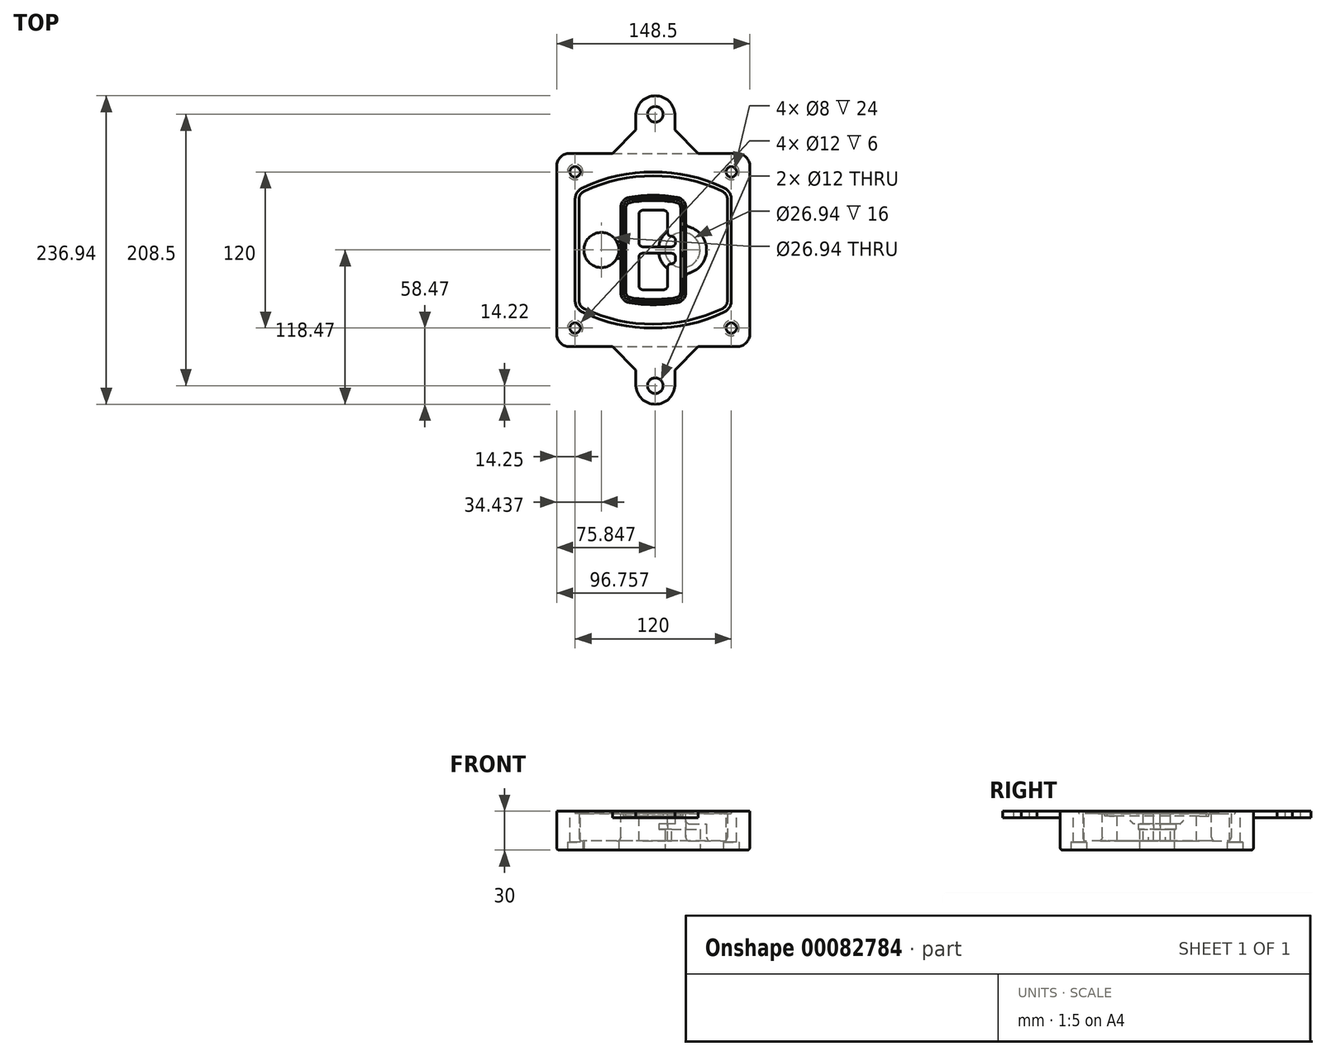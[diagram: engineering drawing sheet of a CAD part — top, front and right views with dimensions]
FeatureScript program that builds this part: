
annotation { "Feature Type Name" : "Feature", "Feature Type Description" : "" }
export const myFeature = defineFeature(function(context is Context, id is Id, definition is map)
    precondition{}
    {
        {
            var Q0;
            Q0=qCreatedBy(makeId("Top.planeOp"),FACE);
            var sketch = newSketch(context, id + "F0", { "sketchPlane" : qUnion([Q0])});
            skPoint(sketch, "E0.rect.middle", {"position": v(0, 0) * mm});
            skLineSegment(sketch, "E1.bottom", {"start": v(-64.25, -74.25) * mm, "end": v(64.25, -74.25) * mm});
            skLineSegment(sketch, "E1.top", {"start": v(-64.25, 74.25) * mm, "end": v(64.25, 74.25) * mm});
            skLineSegment(sketch, "E1.left", {"start": v(-74.25, -64.25) * mm, "end": v(-74.25, 64.25) * mm});
            skLineSegment(sketch, "E1.right", {"start": v(74.25, -64.25) * mm, "end": v(74.25, 64.25) * mm});
            skLineSegment(sketch, "E2", {"start": v(-74.25, 74.25) * mm, "end": v(74.25, -74.25) * mm, "construction": true});
            skLineSegment(sketch, "E3", {"start": v(74.25, 74.25) * mm, "end": v(-74.25, -74.25) * mm, "construction": true});
            skCircle(sketch, "E4", {"center": v(-60, 60) * mm, "radius": 4 * mm});
            skCircle(sketch, "E5", {"center": v(60, 60) * mm, "radius": 4 * mm});
            skCircle(sketch, "E6", {"center": v(60, -60) * mm, "radius": 4 * mm});
            skCircle(sketch, "E7", {"center": v(-60, -60) * mm, "radius": 4 * mm});
            skLineSegment(sketch, "E8", {"start": v(-60, 60) * mm, "end": v(60, 60) * mm, "construction": true});
            skLineSegment(sketch, "E9", {"start": v(60, 60) * mm, "end": v(60, -60) * mm, "construction": true});
            skLineSegment(sketch, "E10", {"start": v(60, -60) * mm, "end": v(-60, -60) * mm, "construction": true});
            skLineSegment(sketch, "E11", {"start": v(-60, -60) * mm, "end": v(-60, 60) * mm, "construction": true});
            skLineSegment(sketch, "E12", {"start": v(-60, 38.83) * mm, "end": v(-60, -38.83) * mm});
            skLineSegment(sketch, "E13", {"start": v(60, 38.83) * mm, "end": v(60, -38.83) * mm});
            skArc(sketch, "E14", {"start": v(54.26, 47.88) * mm, "mid": v(0, 60) * mm, "end": v(-54.26, 47.88) * mm});
            skArc(sketch, "E15", {"start": v(-54.26, -47.88) * mm, "mid": v(0, -60) * mm, "end": v(54.26, -47.88) * mm});
            skLineSegment(sketch, "E16", {"start": v(-60, 0) * mm, "end": v(60, 0) * mm, "construction": true});
            skPoint(sketch, "E17.visualSharp", {"position": v(-60, -45) * mm});
            skArc(sketch, "E17.filletArc", {"start": v(-60, -38.83) * mm, "mid": v(-58.44, -44.2) * mm, "end": v(-54.26, -47.88) * mm});
            skPoint(sketch, "E18.visualSharp", {"position": v(-60, 45) * mm});
            skArc(sketch, "E18.filletArc", {"start": v(-54.26, 47.88) * mm, "mid": v(-58.44, 44.2) * mm, "end": v(-60, 38.83) * mm});
            skPoint(sketch, "E19.visualSharp", {"position": v(60, 45) * mm});
            skArc(sketch, "E19.filletArc", {"start": v(60, 38.83) * mm, "mid": v(58.44, 44.2) * mm, "end": v(54.26, 47.88) * mm});
            skPoint(sketch, "E20.visualSharp", {"position": v(60, -45) * mm});
            skArc(sketch, "E20.filletArc", {"start": v(54.26, -47.88) * mm, "mid": v(58.44, -44.2) * mm, "end": v(60, -38.83) * mm});
            skPoint(sketch, "E21.visualSharp", {"position": v(-74.25, 74.25) * mm});
            skArc(sketch, "E21.filletArc", {"start": v(-64.25, 74.25) * mm, "mid": v(-71.32, 71.32) * mm, "end": v(-74.25, 64.25) * mm});
            skPoint(sketch, "E22.visualSharp", {"position": v(74.25, 74.25) * mm});
            skArc(sketch, "E22.filletArc", {"start": v(74.25, 64.25) * mm, "mid": v(71.32, 71.32) * mm, "end": v(64.25, 74.25) * mm});
            skPoint(sketch, "E23.visualSharp", {"position": v(74.25, -74.25) * mm});
            skArc(sketch, "E23.filletArc", {"start": v(64.25, -74.25) * mm, "mid": v(71.32, -71.32) * mm, "end": v(74.25, -64.25) * mm});
            skPoint(sketch, "E24.visualSharp", {"position": v(-74.25, -74.25) * mm});
            skArc(sketch, "E24.filletArc", {"start": v(-74.25, -64.25) * mm, "mid": v(-71.32, -71.32) * mm, "end": v(-64.25, -74.25) * mm});
            skArc(sketch, "E25.0", {"start": v(57, 38.83) * mm, "mid": v(55.9, 42.58) * mm, "end": v(52.98, 45.17) * mm});
            skLineSegment(sketch, "E25.1", {"start": v(57, 38.83) * mm, "end": v(57, -38.83) * mm});
            skArc(sketch, "E25.2", {"start": v(52.98, -45.17) * mm, "mid": v(55.9, -42.58) * mm, "end": v(57, -38.83) * mm});
            skArc(sketch, "E25.3", {"start": v(-52.98, -45.17) * mm, "mid": v(0, -57) * mm, "end": v(52.98, -45.17) * mm});
            skArc(sketch, "E25.4", {"start": v(-57, -38.83) * mm, "mid": v(-55.9, -42.58) * mm, "end": v(-52.98, -45.17) * mm});
            skArc(sketch, "E25.5", {"start": v(52.98, 45.17) * mm, "mid": v(0, 57) * mm, "end": v(-52.98, 45.17) * mm});
            skLineSegment(sketch, "E25.6", {"start": v(-57, 38.83) * mm, "end": v(-57, -38.83) * mm});
            skArc(sketch, "E25.7", {"start": v(-52.98, 45.17) * mm, "mid": v(-55.9, 42.58) * mm, "end": v(-57, 38.83) * mm});
            skArc(sketch, "E26.0", {"start": v(-55.96, 51.5) * mm, "mid": v(-61.82, 46.33) * mm, "end": v(-64, 38.83) * mm});
            skArc(sketch, "E26.1", {"start": v(55.96, 51.5) * mm, "mid": v(0, 64) * mm, "end": v(-55.96, 51.5) * mm});
            skArc(sketch, "E26.2", {"start": v(64, 38.83) * mm, "mid": v(61.82, 46.33) * mm, "end": v(55.96, 51.5) * mm});
            skLineSegment(sketch, "E26.3", {"start": v(64, 38.83) * mm, "end": v(64, -38.83) * mm});
            skArc(sketch, "E26.4", {"start": v(55.96, -51.5) * mm, "mid": v(61.82, -46.33) * mm, "end": v(64, -38.83) * mm});
            skLineSegment(sketch, "E26.5", {"start": v(-64, 38.83) * mm, "end": v(-64, -38.83) * mm});
            skArc(sketch, "E26.6", {"start": v(-55.96, -51.5) * mm, "mid": v(0, -64) * mm, "end": v(55.96, -51.5) * mm});
            skArc(sketch, "E26.7", {"start": v(-64, -38.83) * mm, "mid": v(-61.82, -46.33) * mm, "end": v(-55.96, -51.5) * mm});
            skSolve(sketch);
        }
        {
            var Q0;
            Q0=makeQuery(id+"F0.imprint","IMPRINT",FACE,{"disambiguationData":[TD([[makeQuery(id+"F0.imprint","IMPRINT",EDGE,{"derivedFrom":sQuery(id+"F0.wireOp",EDGE,"E1.bottom")}),1.0]])]});
            var Q1;
            Q1=makeQuery(id+"F0.imprint","IMPRINT",FACE,{"disambiguationData":[TD([[makeQuery(id+"F0.imprint","IMPRINT",EDGE,{"derivedFrom":sQuery(id+"F0.wireOp",EDGE,"E12")}),1.0]])]});
            var Q2;
            Q2=makeQuery(id+"F0.imprint","IMPRINT",FACE,{"disambiguationData":[TD([[makeQuery(id+"F0.imprint","IMPRINT",EDGE,{"derivedFrom":sQuery(id+"F0.wireOp",EDGE,"E25.0")}),1.0]])]});
            var Q3;
            Q3=makeQuery(id+"F0.imprint","IMPRINT",FACE,{"disambiguationData":[TD([[makeQuery(id+"F0.imprint","IMPRINT",EDGE,{"derivedFrom":sQuery(id+"F0.wireOp",EDGE,"E12")}),-1.0]])]});
            extrude(context, id + "F1", {"entities" : qUnion([Q0, Q1, Q2, Q3]), "oppositeDirection" : true, "depth" : 25 * mm});
        }
        {
            var Q0;
            Q0=makeQuery(id+"F0.imprint","IMPRINT",FACE,{"disambiguationData":[TD([[makeQuery(id+"F0.imprint","IMPRINT",EDGE,{"derivedFrom":sQuery(id+"F0.wireOp",EDGE,"E12")}),1.0]])]});
            extrude(context, id + "F2", {"entities" : qUnion([Q0]), "operationType" : NewBodyOperationType.ADD, "depth" : 3 * mm});
        }
        {
            var Q0;
            Q0=makeQuery(id+"F0.imprint","IMPRINT",FACE,{"disambiguationData":[TD([[makeQuery(id+"F0.imprint","IMPRINT",EDGE,{"derivedFrom":sQuery(id+"F0.wireOp",EDGE,"E25.0")}),1.0]])]});
            extrude(context, id + "F3", {"entities" : qUnion([Q0]), "operationType" : NewBodyOperationType.REMOVE, "oppositeDirection" : true, "depth" : 18 * mm});
        }
        {
            var Q0;
            Q0=makeQuery(id+"F2.opExtrude","CAP_FACE",FACE,{"disambiguationData":[OSD([sQuery(id+"F0.wireOp",EDGE,"E12"),sQuery(id+"F0.wireOp",EDGE,"E13"),sQuery(id+"F0.wireOp",EDGE,"E14"),sQuery(id+"F0.wireOp",EDGE,"E15"),sQuery(id+"F0.wireOp",EDGE,"E17.filletArc"),sQuery(id+"F0.wireOp",EDGE,"E18.filletArc"),sQuery(id+"F0.wireOp",EDGE,"E19.filletArc"),sQuery(id+"F0.wireOp",EDGE,"E20.filletArc"),sQuery(id+"F0.wireOp",EDGE,"E25.0"),sQuery(id+"F0.wireOp",EDGE,"E25.1"),sQuery(id+"F0.wireOp",EDGE,"E25.2"),sQuery(id+"F0.wireOp",EDGE,"E25.3"),sQuery(id+"F0.wireOp",EDGE,"E25.4"),sQuery(id+"F0.wireOp",EDGE,"E25.5"),sQuery(id+"F0.wireOp",EDGE,"E25.6"),sQuery(id+"F0.wireOp",EDGE,"E25.7")])],"isStart":false});
            var sketch = newSketch(context, id + "F4", { "sketchPlane" : qUnion([Q0])});
            skArc(sketch, "E27.0", {"start": v(-18.34, -40.45) * mm, "mid": v(0, -42) * mm, "end": v(18.34, -40.45) * mm});
            skArc(sketch, "E28.0", {"start": v(18.34, 40.45) * mm, "mid": v(0, 42) * mm, "end": v(-18.34, 40.45) * mm});
            skLineSegment(sketch, "E29", {"start": v(-25, 32.57) * mm, "end": v(-25, -32.57) * mm});
            skLineSegment(sketch, "E30", {"start": v(25, 32.57) * mm, "end": v(25, -32.57) * mm});
            skLineSegment(sketch, "E31", {"start": v(-25, 39.1) * mm, "end": v(25, 39.1) * mm, "construction": true});
            skLineSegment(sketch, "E32", {"start": v(-25, -39.1) * mm, "end": v(25, -39.1) * mm, "construction": true});
            skPoint(sketch, "E33.visualSharp", {"position": v(-25, 39.1) * mm});
            skArc(sketch, "E33.filletArc", {"start": v(-18.34, 40.45) * mm, "mid": v(-23.11, 37.73) * mm, "end": v(-25, 32.57) * mm});
            skPoint(sketch, "E34.visualSharp", {"position": v(25, 39.1) * mm});
            skArc(sketch, "E34.filletArc", {"start": v(25, 32.57) * mm, "mid": v(23.11, 37.73) * mm, "end": v(18.34, 40.45) * mm});
            skPoint(sketch, "E35.visualSharp", {"position": v(25, -39.1) * mm});
            skArc(sketch, "E35.filletArc", {"start": v(18.34, -40.45) * mm, "mid": v(23.11, -37.73) * mm, "end": v(25, -32.57) * mm});
            skPoint(sketch, "E36.visualSharp", {"position": v(-25, -39.1) * mm});
            skArc(sketch, "E36.filletArc", {"start": v(-25, -32.57) * mm, "mid": v(-23.11, -37.73) * mm, "end": v(-18.34, -40.45) * mm});
            skArc(sketch, "E37.0", {"start": v(52.98, 45.17) * mm, "mid": v(0, 57) * mm, "end": v(-52.98, 45.17) * mm});
            skArc(sketch, "E37.1", {"start": v(-52.98, 45.17) * mm, "mid": v(-55.9, 42.58) * mm, "end": v(-57, 38.83) * mm});
            skLineSegment(sketch, "E37.2", {"start": v(-57, 38.83) * mm, "end": v(-57, -38.83) * mm});
            skArc(sketch, "E37.3", {"start": v(-57, -38.83) * mm, "mid": v(-55.9, -42.58) * mm, "end": v(-52.98, -45.17) * mm});
            skArc(sketch, "E37.4", {"start": v(-52.98, -45.17) * mm, "mid": v(0, -57) * mm, "end": v(52.98, -45.17) * mm});
            skArc(sketch, "E37.5", {"start": v(52.98, -45.17) * mm, "mid": v(55.9, -42.58) * mm, "end": v(57, -38.83) * mm});
            skLineSegment(sketch, "E37.6", {"start": v(57, 38.83) * mm, "end": v(57, -38.83) * mm});
            skArc(sketch, "E37.7", {"start": v(57, 38.83) * mm, "mid": v(55.9, 42.58) * mm, "end": v(52.98, 45.17) * mm});
            skLineSegment(sketch, "E38.0", {"start": v(23, 32.57) * mm, "end": v(23, -32.57) * mm});
            skArc(sketch, "E38.1", {"start": v(18, -38.48) * mm, "mid": v(21.58, -36.44) * mm, "end": v(23, -32.57) * mm});
            skArc(sketch, "E38.2", {"start": v(-18, -38.48) * mm, "mid": v(0, -40) * mm, "end": v(18, -38.48) * mm});
            skArc(sketch, "E38.3", {"start": v(-23, -32.57) * mm, "mid": v(-21.58, -36.44) * mm, "end": v(-18, -38.48) * mm});
            skLineSegment(sketch, "E38.4", {"start": v(-23, 32.57) * mm, "end": v(-23, -32.57) * mm});
            skArc(sketch, "E38.5", {"start": v(23, 32.57) * mm, "mid": v(21.58, 36.44) * mm, "end": v(18, 38.48) * mm});
            skArc(sketch, "E38.6", {"start": v(-18, 38.48) * mm, "mid": v(-21.58, 36.44) * mm, "end": v(-23, 32.57) * mm});
            skArc(sketch, "E38.7", {"start": v(18, 38.48) * mm, "mid": v(0, 40) * mm, "end": v(-18, 38.48) * mm});
            skArc(sketch, "E39.0", {"start": v(21, 32.57) * mm, "mid": v(20.06, 35.15) * mm, "end": v(17.67, 36.5) * mm});
            skLineSegment(sketch, "E39.1", {"start": v(21, 32.57) * mm, "end": v(21, -32.57) * mm});
            skArc(sketch, "E39.2", {"start": v(17.67, -36.5) * mm, "mid": v(20.06, -35.15) * mm, "end": v(21, -32.57) * mm});
            skArc(sketch, "E39.3", {"start": v(-17.67, -36.5) * mm, "mid": v(0, -38) * mm, "end": v(17.67, -36.5) * mm});
            skArc(sketch, "E39.4", {"start": v(-21, -32.57) * mm, "mid": v(-20.06, -35.15) * mm, "end": v(-17.67, -36.5) * mm});
            skArc(sketch, "E39.5", {"start": v(17.67, 36.5) * mm, "mid": v(0, 38) * mm, "end": v(-17.67, 36.5) * mm});
            skLineSegment(sketch, "E39.6", {"start": v(-21, 32.57) * mm, "end": v(-21, -32.57) * mm});
            skArc(sketch, "E39.7", {"start": v(-17.67, 36.5) * mm, "mid": v(-20.06, 35.15) * mm, "end": v(-21, 32.57) * mm});
            skLineSegment(sketch, "E40", {"start": v(-25, 0) * mm, "end": v(25, 0) * mm, "construction": true});
            skLineSegment(sketch, "E41", {"start": v(-11, 5.5) * mm, "end": v(-11, 27.5) * mm});
            skLineSegment(sketch, "E42", {"start": v(-8, 30.5) * mm, "end": v(8, 30.5) * mm});
            skLineSegment(sketch, "E43", {"start": v(11, 27.5) * mm, "end": v(11, 13.5) * mm});
            skLineSegment(sketch, "E44", {"start": v(14, 10.5) * mm, "end": v(14, 10.5) * mm});
            skLineSegment(sketch, "E45", {"start": v(17, 7.5) * mm, "end": v(17, 5.5) * mm});
            skLineSegment(sketch, "E46", {"start": v(14, 2.5) * mm, "end": v(-8, 2.5) * mm});
            skPoint(sketch, "E47.visualSharp", {"position": v(-11, 30.5) * mm});
            skArc(sketch, "E47.filletArc", {"start": v(-8, 30.5) * mm, "mid": v(-10.12, 29.62) * mm, "end": v(-11, 27.5) * mm});
            skPoint(sketch, "E48.visualSharp", {"position": v(11, 30.5) * mm});
            skArc(sketch, "E48.filletArc", {"start": v(11, 27.5) * mm, "mid": v(10.12, 29.62) * mm, "end": v(8, 30.5) * mm});
            skPoint(sketch, "E49.visualSharp", {"position": v(11, 10.5) * mm});
            skArc(sketch, "E49.filletArc", {"start": v(11, 13.5) * mm, "mid": v(11.88, 11.38) * mm, "end": v(14, 10.5) * mm});
            skPoint(sketch, "E50.visualSharp", {"position": v(17, 10.5) * mm});
            skArc(sketch, "E50.filletArc", {"start": v(17, 7.5) * mm, "mid": v(16.12, 9.62) * mm, "end": v(14, 10.5) * mm});
            skPoint(sketch, "E51.visualSharp", {"position": v(17, 2.5) * mm});
            skArc(sketch, "E51.filletArc", {"start": v(14, 2.5) * mm, "mid": v(16.12, 3.38) * mm, "end": v(17, 5.5) * mm});
            skPoint(sketch, "E52.visualSharp", {"position": v(-11, 2.5) * mm});
            skArc(sketch, "E52.filletArc", {"start": v(-11, 5.5) * mm, "mid": v(-10.12, 3.38) * mm, "end": v(-8, 2.5) * mm});
            skLineSegment(sketch, "E53.0.MirrorCS", {"start": v(14, -2.5) * mm, "end": v(-8, -2.5) * mm});
            skArc(sketch, "E54.0.MirrorCS", {"start": v(-11, -5.5) * mm, "mid": v(-10.12, -3.38) * mm, "end": v(-8, -2.5) * mm});
            skLineSegment(sketch, "E55.0.MirrorCS", {"start": v(-11, -5.5) * mm, "end": v(-11, -27.5) * mm});
            skArc(sketch, "E56.0.MirrorCS", {"start": v(-8, -30.5) * mm, "mid": v(-10.12, -29.62) * mm, "end": v(-11, -27.5) * mm});
            skLineSegment(sketch, "E57.0.MirrorCS", {"start": v(-8, -30.5) * mm, "end": v(8, -30.5) * mm});
            skArc(sketch, "E58.0.MirrorCS", {"start": v(11, -27.5) * mm, "mid": v(10.12, -29.62) * mm, "end": v(8, -30.5) * mm});
            skLineSegment(sketch, "E59.0.MirrorCS", {"start": v(11, -27.5) * mm, "end": v(11, -13.5) * mm});
            skArc(sketch, "E60.0.MirrorCS", {"start": v(11, -13.5) * mm, "mid": v(11.88, -11.38) * mm, "end": v(14, -10.5) * mm});
            skArc(sketch, "E61.0.MirrorCS", {"start": v(17, -7.5) * mm, "mid": v(16.12, -9.62) * mm, "end": v(14, -10.5) * mm});
            skLineSegment(sketch, "E62.0.MirrorCS", {"start": v(17, -7.5) * mm, "end": v(17, -5.5) * mm});
            skArc(sketch, "E63.0.MirrorCS", {"start": v(14, -2.5) * mm, "mid": v(16.12, -3.38) * mm, "end": v(17, -5.5) * mm});
            skSolve(sketch);
        }
        {
            var Q0;
            Q0=makeQuery(id+"F4.imprint","IMPRINT",FACE,{"disambiguationData":[TD([[makeQuery(id+"F4.imprint","IMPRINT",EDGE,{"derivedFrom":sQuery(id+"F4.wireOp",EDGE,"E27.0")}),1.0]])]});
            var Q1;
            Q1=makeQuery(id+"F4.imprint","IMPRINT",FACE,{"disambiguationData":[TD([[makeQuery(id+"F4.imprint","IMPRINT",EDGE,{"derivedFrom":sQuery(id+"F4.wireOp",EDGE,"E38.0")}),-1.0]])]});
            var Q2;
            Q2=makeQuery(id+"F4.imprint","IMPRINT",FACE,{"disambiguationData":[TD([[makeQuery(id+"F4.imprint","IMPRINT",EDGE,{"derivedFrom":sQuery(id+"F4.wireOp",EDGE,"E39.0")}),1.0]])]});
            extrude(context, id + "F5", {"entities" : qUnion([Q0, Q1, Q2]), "operationType" : NewBodyOperationType.ADD, "endBound" : BoundingType.UP_TO_NEXT, "oppositeDirection" : true, "depth" : 25 * mm});
        }
        {
            var Q0;
            Q0=makeQuery(id+"F4.imprint","IMPRINT",FACE,{"disambiguationData":[TD([[makeQuery(id+"F4.imprint","IMPRINT",EDGE,{"derivedFrom":sQuery(id+"F4.wireOp",EDGE,"E38.0")}),-1.0]])]});
            extrude(context, id + "F6", {"entities" : qUnion([Q0]), "operationType" : NewBodyOperationType.REMOVE, "oppositeDirection" : true, "depth" : 2 * mm});
        }
        {
            var Q0;
            Q0=makeQuery(id+"F1.opExtrude","CAP_FACE",FACE,{"disambiguationData":[OSD([sQuery(id+"F0.wireOp",EDGE,"E1.bottom"),sQuery(id+"F0.wireOp",EDGE,"E1.top"),sQuery(id+"F0.wireOp",EDGE,"E1.left"),sQuery(id+"F0.wireOp",EDGE,"E1.right"),sQuery(id+"F0.wireOp",EDGE,"E4"),sQuery(id+"F0.wireOp",EDGE,"E5"),sQuery(id+"F0.wireOp",EDGE,"E6"),sQuery(id+"F0.wireOp",EDGE,"E7"),sQuery(id+"F0.wireOp",EDGE,"E21.filletArc"),sQuery(id+"F0.wireOp",EDGE,"E22.filletArc"),sQuery(id+"F0.wireOp",EDGE,"E23.filletArc"),sQuery(id+"F0.wireOp",EDGE,"E24.filletArc")])],"isStart":false});
            var sketch = newSketch(context, id + "F7", { "sketchPlane" : qUnion([Q0])});
            skCircle(sketch, "E64", {"center": v(22.5, 0) * mm, "radius": 13.47 * mm});
            skCircle(sketch, "E65", {"center": v(-39.81, 0) * mm, "radius": 13.47 * mm});
            skLineSegment(sketch, "E66", {"start": v(74.25, 0) * mm, "end": v(-74.25, 0) * mm});
            skCircle(sketch, "E67", {"center": v(22.5, 0) * mm, "radius": 18.47 * mm});
            skCircle(sketch, "E68", {"center": v(60, -60) * mm, "radius": 6 * mm});
            skCircle(sketch, "E69", {"center": v(-60, -60) * mm, "radius": 6 * mm});
            skCircle(sketch, "E70", {"center": v(-60, 60) * mm, "radius": 6 * mm});
            skCircle(sketch, "E71", {"center": v(60, 60) * mm, "radius": 6 * mm});
            skSolve(sketch);
        }
        {
            var Q0;
            {var subQ1=sQuery(id+"F7.wireOp",EDGE,"E66");var subQ4=sQuery(id+"F7.wireOp",EDGE,"E64");var subQ6=makeQuery(id+"F7.imprint","INTERSECT",VERTEX,{"disambiguationData":[OD(0.0)],"derivedFrom":[subQ4,subQ1]});Q0=makeQuery(id+"F7.imprint","IMPRINT",FACE,{"disambiguationData":[TD([[makeQuery(id+"F7.imprint","IMPRINT",EDGE,{"disambiguationData":[TD([[subQ6,-1.0]])],"derivedFrom":subQ4}),-1.0]])]});}
            var Q1;
            {var subQ0=sQuery(id+"F7.wireOp",EDGE,"E66");var subQ1=sQuery(id+"F7.wireOp",EDGE,"E64");var subQ3=makeQuery(id+"F7.imprint","INTERSECT",VERTEX,{"disambiguationData":[OD(0.0)],"derivedFrom":[subQ1,subQ0]});Q1=makeQuery(id+"F7.imprint","IMPRINT",FACE,{"disambiguationData":[TD([[makeQuery(id+"F7.imprint","IMPRINT",EDGE,{"disambiguationData":[TD([[subQ3,-1.0]])],"derivedFrom":subQ1}),1.0]])]});}
            var Q2;
            {var subQ0=sQuery(id+"F7.wireOp",EDGE,"E66");var subQ1=sQuery(id+"F7.wireOp",EDGE,"E64");var subQ3=makeQuery(id+"F7.imprint","INTERSECT",VERTEX,{"disambiguationData":[OD(0.0)],"derivedFrom":[subQ1,subQ0]});Q2=makeQuery(id+"F7.imprint","IMPRINT",FACE,{"disambiguationData":[TD([[makeQuery(id+"F7.imprint","IMPRINT",EDGE,{"disambiguationData":[TD([[subQ3,1.0]])],"derivedFrom":subQ1}),1.0]])]});}
            var Q3;
            {var subQ1=sQuery(id+"F7.wireOp",EDGE,"E66");var subQ4=sQuery(id+"F7.wireOp",EDGE,"E64");var subQ6=makeQuery(id+"F7.imprint","INTERSECT",VERTEX,{"disambiguationData":[OD(0.0)],"derivedFrom":[subQ4,subQ1]});Q3=makeQuery(id+"F7.imprint","IMPRINT",FACE,{"disambiguationData":[TD([[makeQuery(id+"F7.imprint","IMPRINT",EDGE,{"disambiguationData":[TD([[subQ6,1.0]])],"derivedFrom":subQ4}),-1.0]])]});}
            extrude(context, id + "F8", {"entities" : qUnion([Q0, Q1, Q2, Q3]), "operationType" : NewBodyOperationType.ADD, "oppositeDirection" : true, "depth" : 20 * mm});
        }
        {
            var Q0;
            {var subQ0=sQuery(id+"F7.wireOp",EDGE,"E66");var subQ1=sQuery(id+"F7.wireOp",EDGE,"E64");var subQ3=makeQuery(id+"F7.imprint","INTERSECT",VERTEX,{"disambiguationData":[OD(0.0)],"derivedFrom":[subQ1,subQ0]});Q0=makeQuery(id+"F7.imprint","IMPRINT",FACE,{"disambiguationData":[TD([[makeQuery(id+"F7.imprint","IMPRINT",EDGE,{"disambiguationData":[TD([[subQ3,-1.0]])],"derivedFrom":subQ1}),1.0]])]});}
            var Q1;
            {var subQ0=sQuery(id+"F7.wireOp",EDGE,"E66");var subQ1=sQuery(id+"F7.wireOp",EDGE,"E64");var subQ3=makeQuery(id+"F7.imprint","INTERSECT",VERTEX,{"disambiguationData":[OD(0.0)],"derivedFrom":[subQ1,subQ0]});Q1=makeQuery(id+"F7.imprint","IMPRINT",FACE,{"disambiguationData":[TD([[makeQuery(id+"F7.imprint","IMPRINT",EDGE,{"disambiguationData":[TD([[subQ3,1.0]])],"derivedFrom":subQ1}),1.0]])]});}
            extrude(context, id + "F9", {"entities" : qUnion([Q0, Q1]), "operationType" : NewBodyOperationType.REMOVE, "oppositeDirection" : true, "depth" : 16 * mm});
        }
        {
            var Q0;
            {var subQ0=sQuery(id+"F7.wireOp",EDGE,"E66");var subQ1=sQuery(id+"F7.wireOp",EDGE,"E65");var subQ3=makeQuery(id+"F7.imprint","INTERSECT",VERTEX,{"disambiguationData":[OD(0.0)],"derivedFrom":[subQ1,subQ0]});Q0=makeQuery(id+"F7.imprint","IMPRINT",FACE,{"disambiguationData":[TD([[makeQuery(id+"F7.imprint","IMPRINT",EDGE,{"disambiguationData":[TD([[subQ3,-1.0]])],"derivedFrom":subQ1}),1.0]])]});}
            var Q1;
            {var subQ0=sQuery(id+"F7.wireOp",EDGE,"E66");var subQ1=sQuery(id+"F7.wireOp",EDGE,"E65");var subQ3=makeQuery(id+"F7.imprint","INTERSECT",VERTEX,{"disambiguationData":[OD(0.0)],"derivedFrom":[subQ1,subQ0]});Q1=makeQuery(id+"F7.imprint","IMPRINT",FACE,{"disambiguationData":[TD([[makeQuery(id+"F7.imprint","IMPRINT",EDGE,{"disambiguationData":[TD([[subQ3,1.0]])],"derivedFrom":subQ1}),1.0]])]});}
            extrude(context, id + "F10", {"entities" : qUnion([Q0, Q1]), "operationType" : NewBodyOperationType.REMOVE, "oppositeDirection" : true, "depth" : 25 * mm});
        }
        {
            var Q0;
            Q0=makeQuery(id+"F7.imprint","IMPRINT",FACE,{"disambiguationData":[TD([[makeQuery(id+"F7.imprint","IMPRINT",EDGE,{"derivedFrom":sQuery(id+"F7.wireOp",EDGE,"E68")}),1.0]])]});
            var Q1;
            Q1=makeQuery(id+"F7.imprint","IMPRINT",FACE,{"disambiguationData":[TD([[makeQuery(id+"F7.imprint","IMPRINT",EDGE,{"derivedFrom":makeQuery(id+"F1.opExtrude","CAP_EDGE",EDGE,{"disambiguationData":[OSD([sQuery(id+"F0.wireOp",EDGE,"E5")])],"isStart":false})}),-1.0]])]});
            var Q2;
            Q2=makeQuery(id+"F7.imprint","IMPRINT",FACE,{"disambiguationData":[TD([[makeQuery(id+"F7.imprint","IMPRINT",EDGE,{"derivedFrom":sQuery(id+"F7.wireOp",EDGE,"E69")}),1.0]])]});
            var Q3;
            Q3=makeQuery(id+"F7.imprint","IMPRINT",FACE,{"disambiguationData":[TD([[makeQuery(id+"F7.imprint","IMPRINT",EDGE,{"derivedFrom":makeQuery(id+"F1.opExtrude","CAP_EDGE",EDGE,{"disambiguationData":[OSD([sQuery(id+"F0.wireOp",EDGE,"E4")])],"isStart":false})}),-1.0]])]});
            var Q4;
            Q4=makeQuery(id+"F7.imprint","IMPRINT",FACE,{"disambiguationData":[TD([[makeQuery(id+"F7.imprint","IMPRINT",EDGE,{"derivedFrom":sQuery(id+"F7.wireOp",EDGE,"E70")}),1.0]])]});
            var Q5;
            Q5=makeQuery(id+"F7.imprint","IMPRINT",FACE,{"disambiguationData":[TD([[makeQuery(id+"F7.imprint","IMPRINT",EDGE,{"derivedFrom":makeQuery(id+"F1.opExtrude","CAP_EDGE",EDGE,{"disambiguationData":[OSD([sQuery(id+"F0.wireOp",EDGE,"E7")])],"isStart":false})}),-1.0]])]});
            var Q6;
            Q6=makeQuery(id+"F7.imprint","IMPRINT",FACE,{"disambiguationData":[TD([[makeQuery(id+"F7.imprint","IMPRINT",EDGE,{"derivedFrom":sQuery(id+"F7.wireOp",EDGE,"E71")}),1.0]])]});
            var Q7;
            Q7=makeQuery(id+"F7.imprint","IMPRINT",FACE,{"disambiguationData":[TD([[makeQuery(id+"F7.imprint","IMPRINT",EDGE,{"derivedFrom":makeQuery(id+"F1.opExtrude","CAP_EDGE",EDGE,{"disambiguationData":[OSD([sQuery(id+"F0.wireOp",EDGE,"E6")])],"isStart":false})}),-1.0]])]});
            extrude(context, id + "F11", {"entities" : qUnion([Q0, Q1, Q2, Q3, Q4, Q5, Q6, Q7]), "operationType" : NewBodyOperationType.REMOVE, "oppositeDirection" : true, "depth" : 6 * mm});
        }
        {
            var Q0;
            Q0=makeQuery(id+"F9.boolean.opBoolean","COPY",FACE,{"derivedFrom":makeQuery(id+"F9.opExtrude","CAP_FACE",FACE,{"disambiguationData":[OSD([sQuery(id+"F7.wireOp",EDGE,"E64")])],"isStart":false})});
            var sketch = newSketch(context, id + "F12", { "sketchPlane" : qUnion([Q0])});
            skArc(sketch, "E72.0", {"start": v(11, 14.45) * mm, "mid": v(6.45, 9.13) * mm, "end": v(4.2, 2.5) * mm});
            skArc(sketch, "E72.1", {"start": v(4.2, -2.5) * mm, "mid": v(6.45, -9.13) * mm, "end": v(11, -14.45) * mm});
            skLineSegment(sketch, "E73", {"start": v(4.2, -2.5) * mm, "end": v(14, -2.5) * mm});
            skLineSegment(sketch, "E74.0", {"start": v(14, 2.5) * mm, "end": v(4.2, 2.5) * mm});
            skArc(sketch, "E74.1", {"start": v(14, 2.5) * mm, "mid": v(16.12, 3.38) * mm, "end": v(17, 5.5) * mm});
            skLineSegment(sketch, "E74.2", {"start": v(17, 7.5) * mm, "end": v(17, 5.5) * mm});
            skArc(sketch, "E74.3", {"start": v(17, 7.5) * mm, "mid": v(16.12, 9.62) * mm, "end": v(14, 10.5) * mm});
            skArc(sketch, "E74.4", {"start": v(11, 13.5) * mm, "mid": v(11.88, 11.38) * mm, "end": v(14, 10.5) * mm});
            skLineSegment(sketch, "E74.5", {"start": v(11, 14.45) * mm, "end": v(11, 13.5) * mm});
            skLineSegment(sketch, "E74.7", {"start": v(14, -2.5) * mm, "end": v(4.2, -2.5) * mm});
            skArc(sketch, "E74.8", {"start": v(14, -2.5) * mm, "mid": v(16.12, -3.38) * mm, "end": v(17, -5.5) * mm});
            skLineSegment(sketch, "E74.9", {"start": v(17, -7.5) * mm, "end": v(17, -5.5) * mm});
            skArc(sketch, "E74.10", {"start": v(17, -7.5) * mm, "mid": v(16.12, -9.62) * mm, "end": v(14, -10.5) * mm});
            skArc(sketch, "E74.11", {"start": v(11, -13.5) * mm, "mid": v(11.88, -11.38) * mm, "end": v(14, -10.5) * mm});
            skLineSegment(sketch, "E74.12", {"start": v(11, -14.45) * mm, "end": v(11, -13.5) * mm});
            skPoint(sketch, "E75.orphan", {"position": v(11, -27.5) * mm});
            skPoint(sketch, "E76.orphan", {"position": v(-8, -2.5) * mm});
            skPoint(sketch, "E77.orphan", {"position": v(-8, 2.5) * mm});
            skPoint(sketch, "E78.orphan", {"position": v(11, 27.5) * mm});
            skSolve(sketch);
        }
        {
            var Q0;
            {var subQ7=sQuery(id+"F12.wireOp",EDGE,"E72.0");var subQ14=sQuery(id+"F12.wireOp",EDGE,"E72.1");var subQ16=sQuery(id+"F12.wireOp",EDGE,"E74.1");var subQ18=sQuery(id+"F12.wireOp",EDGE,"E74.8");Q0=qUnion([makeQuery(id+"F12.imprint","IMPRINT",FACE,{"disambiguationData":[TD([[makeQuery(id+"F12.imprint","IMPRINT",EDGE,{"derivedFrom":subQ7}),1.0]])]}),makeQuery(id+"F12.imprint","IMPRINT",FACE,{"disambiguationData":[TD([[makeQuery(id+"F12.imprint","IMPRINT",EDGE,{"derivedFrom":subQ14}),1.0]])]}),makeQuery(id+"F12.imprint","IMPRINT",FACE,{"disambiguationData":[TD([[makeQuery(id+"F12.imprint","IMPRINT",EDGE,{"derivedFrom":subQ16}),1.0]])]}),makeQuery(id+"F12.imprint","IMPRINT",FACE,{"disambiguationData":[TD([[makeQuery(id+"F12.imprint","IMPRINT",EDGE,{"derivedFrom":subQ18}),-1.0]])]})]);}
            var Q1;
            Q1=makeQuery(id+"F5.boolean.opBoolean","SPLIT",FACE,{"disambiguationData":[TD([makeQuery(id+"F5.opExtrude","SWEPT_FACE",FACE,{"disambiguationData":[OSD([sQuery(id+"F4.wireOp",EDGE,"E41")])]})])],"derivedFrom":makeQuery(id+"F3.boolean.opBoolean","COPY",FACE,{"derivedFrom":makeQuery(id+"F3.opExtrude","CAP_FACE",FACE,{"disambiguationData":[OSD([sQuery(id+"F0.wireOp",EDGE,"E25.0"),sQuery(id+"F0.wireOp",EDGE,"E25.1"),sQuery(id+"F0.wireOp",EDGE,"E25.2"),sQuery(id+"F0.wireOp",EDGE,"E25.3"),sQuery(id+"F0.wireOp",EDGE,"E25.4"),sQuery(id+"F0.wireOp",EDGE,"E25.5"),sQuery(id+"F0.wireOp",EDGE,"E25.6"),sQuery(id+"F0.wireOp",EDGE,"E25.7")])],"isStart":false})})});
            extrude(context, id + "F13", {"entities" : qUnion([Q0]), "operationType" : NewBodyOperationType.REMOVE, "endBound" : BoundingType.UP_TO_SURFACE, "endBoundEntityFace" : qUnion([Q1]), "depth" : 25 * mm});
        }
        {
            var Q0;
            Q0=makeQuery(id+"F3.boolean.opBoolean","COPY",EDGE,{"derivedFrom":makeQuery(id+"F3.opExtrude","CAP_EDGE",EDGE,{"disambiguationData":[OSD([sQuery(id+"F0.wireOp",EDGE,"E25.6")])],"isStart":false})});
            var Q1;
            Q1=makeQuery(id+"F8.boolean.opBoolean","INTERSECT",EDGE,{"derivedFrom":[makeQuery(id+"F5.opExtrude","SWEPT_FACE",FACE,{"disambiguationData":[OSD([sQuery(id+"F4.wireOp",EDGE,"E30")])]}),makeQuery(id+"F8.opExtrude","CAP_FACE",FACE,{"disambiguationData":[OSD([sQuery(id+"F7.wireOp",EDGE,"E67")])],"isStart":false})]});
            var Q2;
            Q2=makeQuery(id+"F8.boolean.opBoolean","INTERSECT",EDGE,{"disambiguationData":[OD(1.0)],"derivedFrom":[makeQuery(id+"F5.opExtrude","SWEPT_FACE",FACE,{"disambiguationData":[OSD([sQuery(id+"F4.wireOp",EDGE,"E30")])]}),makeQuery(id+"F8.opExtrude","SWEPT_FACE",FACE,{"disambiguationData":[OSD([sQuery(id+"F7.wireOp",EDGE,"E67")])]})]});
            var Q3;
            {var subQ0=sQuery(id+"F4.wireOp",EDGE,"E30");Q3=makeQuery(id+"F8.boolean.opBoolean","SPLIT",EDGE,{"disambiguationData":[TD([makeQuery(id+"F5.opExtrude","SWEPT_FACE",FACE,{"disambiguationData":[OSD([sQuery(id+"F4.wireOp",EDGE,"E35.filletArc")])]})])],"derivedFrom":makeQuery(id+"F5.opExtrude","CAP_EDGE",EDGE,{"disambiguationData":[OSD([subQ0])],"isStart":false})});}
            var Q4;
            {var subQ0=sQuery(id+"F0.wireOp",EDGE,"E25.7");var subQ1=sQuery(id+"F0.wireOp",EDGE,"E25.1");var subQ2=sQuery(id+"F0.wireOp",EDGE,"E25.6");var subQ3=sQuery(id+"F0.wireOp",EDGE,"E25.5");var subQ4=sQuery(id+"F0.wireOp",EDGE,"E25.4");var subQ5=sQuery(id+"F0.wireOp",EDGE,"E25.0");var subQ6=sQuery(id+"F0.wireOp",EDGE,"E25.2");var subQ7=sQuery(id+"F0.wireOp",EDGE,"E25.3");Q4=makeQuery(id+"F8.boolean.opBoolean","INTERSECT",EDGE,{"derivedFrom":[makeQuery(id+"F5.boolean.opBoolean","SPLIT",FACE,{"disambiguationData":[TD([makeQuery(id+"F2.opExtrude","SWEPT_FACE",FACE,{"disambiguationData":[OSD([subQ5])]})])],"derivedFrom":makeQuery(id+"F3.boolean.opBoolean","COPY",FACE,{"derivedFrom":makeQuery(id+"F3.opExtrude","CAP_FACE",FACE,{"disambiguationData":[OSD([subQ5,subQ1,subQ6,subQ7,subQ4,subQ3,subQ2,subQ0])],"isStart":false})})}),makeQuery(id+"F8.opExtrude","SWEPT_FACE",FACE,{"disambiguationData":[OSD([sQuery(id+"F7.wireOp",EDGE,"E67")])]})]});}
            var Q5;
            Q5=makeQuery(id+"F8.boolean.opBoolean","INTERSECT",EDGE,{"disambiguationData":[OD(0.0)],"derivedFrom":[makeQuery(id+"F5.opExtrude","SWEPT_FACE",FACE,{"disambiguationData":[OSD([sQuery(id+"F4.wireOp",EDGE,"E30")])]}),makeQuery(id+"F8.opExtrude","SWEPT_FACE",FACE,{"disambiguationData":[OSD([sQuery(id+"F7.wireOp",EDGE,"E67")])]})]});
            fillet(context, id + "F14", {"entities" : qUnion([Q0, Q1, Q2, Q3, Q4, Q5]), "radius" : 3 * mm, "tangentPropagation" : true, "allowEdgeOverflow" : false});
        }
        {
            var Q0;
            Q0=makeQuery(id+"F1.opExtrude","CAP_EDGE",EDGE,{"disambiguationData":[OSD([sQuery(id+"F0.wireOp",EDGE,"E1.bottom")])],"isStart":false});
            fillet(context, id + "F15", {"entities" : qUnion([Q0]), "radius" : 2 * mm, "tangentPropagation" : true, "allowEdgeOverflow" : false});
        }
        {
            var Q0;
            {var subQ0=sQuery(id+"F0.wireOp",EDGE,"E22.filletArc");var subQ1=sQuery(id+"F0.wireOp",EDGE,"E7");var subQ2=sQuery(id+"F0.wireOp",EDGE,"E6");var subQ3=sQuery(id+"F0.wireOp",EDGE,"E5");var subQ4=sQuery(id+"F0.wireOp",EDGE,"E4");var subQ5=sQuery(id+"F0.wireOp",EDGE,"E1.bottom");var subQ6=sQuery(id+"F0.wireOp",EDGE,"E21.filletArc");var subQ7=sQuery(id+"F0.wireOp",EDGE,"E1.top");var subQ8=sQuery(id+"F0.wireOp",EDGE,"E1.left");var subQ9=sQuery(id+"F0.wireOp",EDGE,"E1.right");var subQ10=sQuery(id+"F0.wireOp",EDGE,"E23.filletArc");var subQ11=sQuery(id+"F0.wireOp",EDGE,"E24.filletArc");Q0=makeQuery(id+"F2.boolean.opBoolean","SPLIT",FACE,{"disambiguationData":[TD([makeQuery(id+"F1.opExtrude","SWEPT_FACE",FACE,{"disambiguationData":[OSD([subQ5])]})])],"derivedFrom":makeQuery(id+"F1.opExtrude","CAP_FACE",FACE,{"disambiguationData":[OSD([subQ5,subQ7,subQ8,subQ9,subQ4,subQ3,subQ2,subQ1,subQ6,subQ0,subQ10,subQ11])],"isStart":true})});}
            var sketch = newSketch(context, id + "F16", { "sketchPlane" : qUnion([Q0])});
            skLineSegment(sketch, "E79", {"start": v(0, 74.25) * mm, "end": v(1.6, -74.25) * mm, "construction": true});
            skLineSegment(sketch, "E80", {"start": v(1.6, -74.25) * mm, "end": v(1.6, -104.25) * mm, "construction": true});
            skCircle(sketch, "E81", {"center": v(1.6, -104.25) * mm, "radius": 6 * mm});
            skLineSegment(sketch, "E82", {"start": v(34.58, -74.25) * mm, "end": v(16.58, -92.25) * mm});
            skLineSegment(sketch, "E83", {"start": v(-31.38, -74.25) * mm, "end": v(-13.38, -92.25) * mm});
            skLineSegment(sketch, "E84", {"start": v(16.58, -92.25) * mm, "end": v(16.58, -104.25) * mm});
            skLineSegment(sketch, "E85", {"start": v(-13.38, -92.25) * mm, "end": v(-13.38, -104.25) * mm});
            skArc(sketch, "E86", {"start": v(-13.38, -104.25) * mm, "mid": v(1.6, -118.47) * mm, "end": v(16.58, -104.25) * mm});
            skLineSegment(sketch, "E87", {"start": v(74.25, 0) * mm, "end": v(-74.25, 0) * mm, "construction": true});
            skLineSegment(sketch, "E88.MirrorCS", {"start": v(34.58, 74.25) * mm, "end": v(16.58, 92.25) * mm});
            skArc(sketch, "E89.MirrorCS", {"start": v(-13.38, 104.25) * mm, "mid": v(1.6, 118.47) * mm, "end": v(16.58, 104.25) * mm});
            skLineSegment(sketch, "E90.MirrorCS", {"start": v(-31.38, 74.25) * mm, "end": v(-13.38, 92.25) * mm});
            skLineSegment(sketch, "E91.MirrorCS", {"start": v(-13.38, 92.25) * mm, "end": v(-13.38, 104.25) * mm});
            skLineSegment(sketch, "E92.MirrorCS", {"start": v(16.58, 92.25) * mm, "end": v(16.58, 104.25) * mm});
            skCircle(sketch, "E93.MirrorC", {"center": v(1.6, 104.25) * mm, "radius": 6 * mm});
            skSolve(sketch);
        }
        {
            var Q0;
            Q0=makeQuery(id+"F16.imprint","IMPRINT",FACE,{"disambiguationData":[TD([[makeQuery(id+"F16.imprint","IMPRINT",EDGE,{"derivedFrom":sQuery(id+"F16.wireOp",EDGE,"E81")}),-1.0]])]});
            var Q1;
            Q1=makeQuery(id+"F16.imprint","IMPRINT",FACE,{"disambiguationData":[TD([[makeQuery(id+"F16.imprint","IMPRINT",EDGE,{"derivedFrom":makeQuery(id+"F1.opExtrude","CAP_EDGE",EDGE,{"disambiguationData":[OSD([sQuery(id+"F0.wireOp",EDGE,"E1.left")])],"isStart":true})}),-1.0]])]});
            var Q2;
            {var subQ1=sQuery(id+"F16.wireOp",EDGE,"E88.MirrorCS");Q2=makeQuery(id+"F16.imprint","IMPRINT",FACE,{"disambiguationData":[TD([[makeQuery(id+"F16.imprint","IMPRINT",EDGE,{"derivedFrom":subQ1}),1.0]])]});}
            extrude(context, id + "F17", {"entities" : qUnion([Q0, Q1, Q2]), "operationType" : NewBodyOperationType.ADD, "depth" : 5 * mm});
        }
    });
